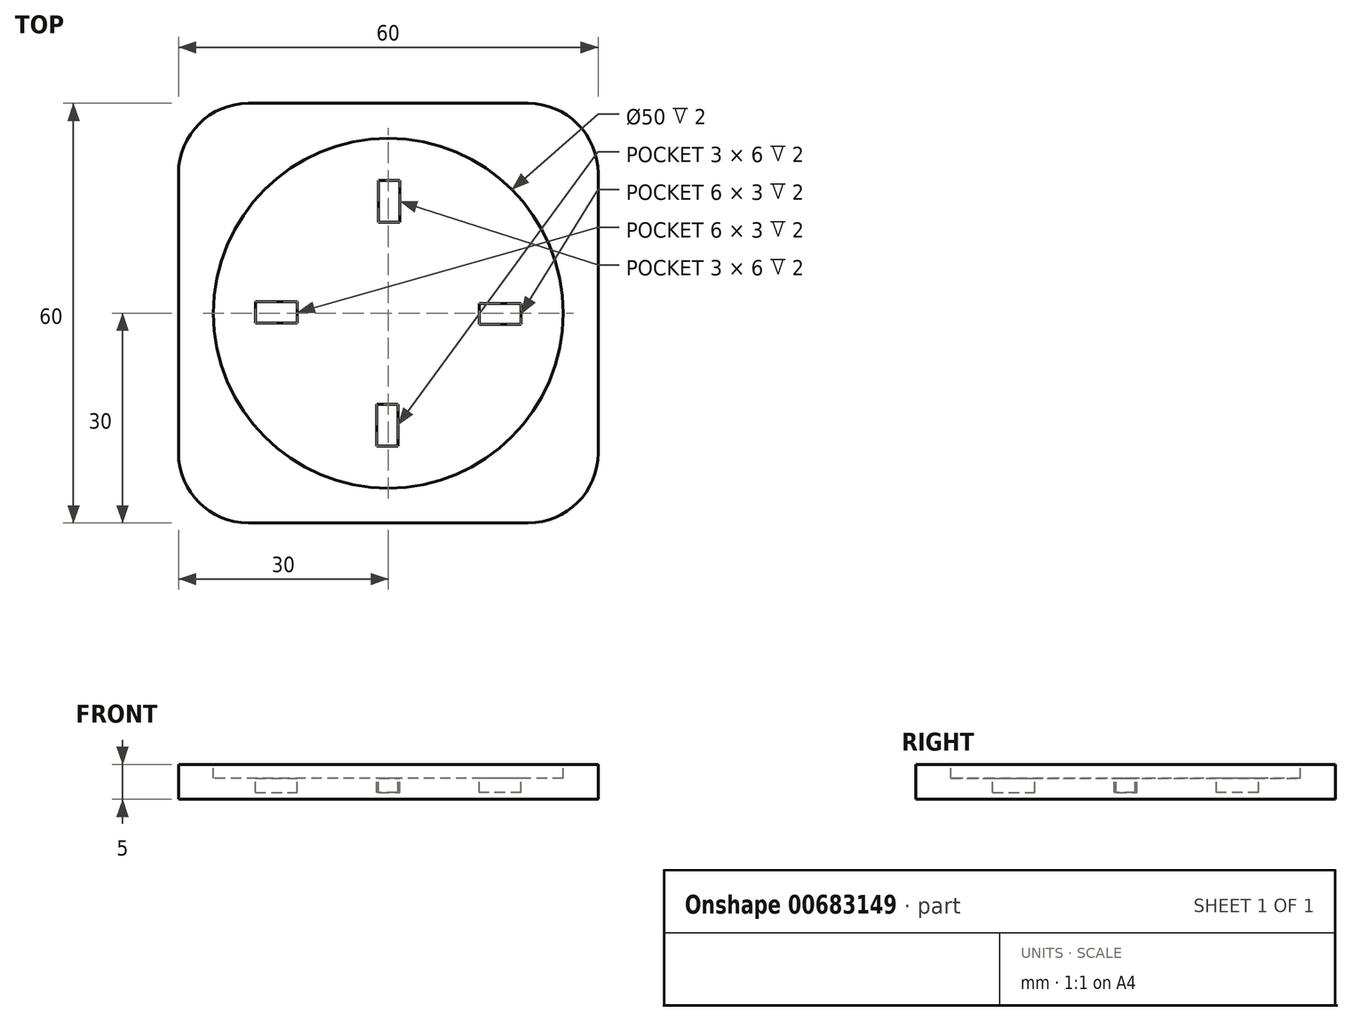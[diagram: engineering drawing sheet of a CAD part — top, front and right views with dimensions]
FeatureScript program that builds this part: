
annotation { "Feature Type Name" : "Feature", "Feature Type Description" : "" }
export const myFeature = defineFeature(function(context is Context, id is Id, definition is map)
    precondition{}
    {
        {
            var Q0;
            Q0=qCreatedBy(makeId("Top.planeOp"),FACE);
            var sketch = newSketch(context, id + "F0", { "sketchPlane" : qUnion([Q0])});
            skLineSegment(sketch, "E0.bottom", {"start": v(-20, 30) * mm, "end": v(20, 30) * mm});
            skLineSegment(sketch, "E0.top", {"start": v(-20, -30) * mm, "end": v(20, -30) * mm});
            skLineSegment(sketch, "E0.left", {"start": v(-30, 20) * mm, "end": v(-30, -20) * mm});
            skLineSegment(sketch, "E0.right", {"start": v(30, 20) * mm, "end": v(30, -20) * mm});
            skPoint(sketch, "E0.middle", {"position": v(0, 0) * mm});
            skPoint(sketch, "E1.visualSharp", {"position": v(-30, 30) * mm});
            skArc(sketch, "E1.filletArc", {"start": v(-20, 30) * mm, "mid": v(-27.07, 27.07) * mm, "end": v(-30, 20) * mm});
            skPoint(sketch, "E2.visualSharp", {"position": v(30, 30) * mm});
            skArc(sketch, "E2.filletArc", {"start": v(30, 20) * mm, "mid": v(27.07, 27.07) * mm, "end": v(20, 30) * mm});
            skPoint(sketch, "E3.visualSharp", {"position": v(-30, -30) * mm});
            skArc(sketch, "E3.filletArc", {"start": v(-30, -20) * mm, "mid": v(-27.07, -27.07) * mm, "end": v(-20, -30) * mm});
            skPoint(sketch, "E4.visualSharp", {"position": v(30, -30) * mm});
            skArc(sketch, "E4.filletArc", {"start": v(20, -30) * mm, "mid": v(27.07, -27.07) * mm, "end": v(30, -20) * mm});
            skSolve(sketch);
        }
        {
            var Q0;
            Q0=makeQuery(id+"F0.imprint","IMPRINT",FACE,{"disambiguationData":[TD([[makeQuery(id+"F0.imprint","IMPRINT",EDGE,{"derivedFrom":sQuery(id+"F0.wireOp",EDGE,"E0.bottom")}),-1.0]])]});
            extrude(context, id + "F1", {"entities" : qUnion([Q0]), "depth" : 5 * mm, "offsetDistance" : 25.4 * mm});
        }
        {
            var Q0;
            Q0=makeQuery(id+"F1.opExtrude","CAP_FACE",FACE,{"disambiguationData":[OSD([sQuery(id+"F0.wireOp",EDGE,"E0.bottom"),sQuery(id+"F0.wireOp",EDGE,"E0.top"),sQuery(id+"F0.wireOp",EDGE,"E0.left"),sQuery(id+"F0.wireOp",EDGE,"E0.right")])],"isStart":false});
            var sketch = newSketch(context, id + "F2", { "sketchPlane" : qUnion([Q0])});
            skCircle(sketch, "E5", {"center": v(0, 0) * mm, "radius": 25 * mm});
            skSolve(sketch);
        }
        {
            var Q0;
            Q0 = qSketchRegion(id + "F2", true);
            extrude(context, id + "F3", {"entities" : qUnion([Q0]), "operationType" : NewBodyOperationType.REMOVE, "oppositeDirection" : true, "depth" : 2 * mm, "offsetDistance" : 25.4 * mm});
        }
        {
            var Q0;
            Q0=makeQuery(id+"F3.boolean.opBoolean","COPY",FACE,{"derivedFrom":makeQuery(id+"F3.opExtrude","CAP_FACE",FACE,{"disambiguationData":[OSD([sQuery(id+"F2.wireOp",EDGE,"E5")])],"isStart":false})});
            var sketch = newSketch(context, id + "F4", { "sketchPlane" : qUnion([Q0])});
            skLineSegment(sketch, "E6.bottom", {"start": v(-1.37, 19) * mm, "end": v(1.63, 19) * mm});
            skLineSegment(sketch, "E6.top", {"start": v(-1.37, 13) * mm, "end": v(1.63, 13) * mm});
            skLineSegment(sketch, "E6.left", {"start": v(-1.37, 19) * mm, "end": v(-1.37, 13) * mm});
            skLineSegment(sketch, "E6.right", {"start": v(1.63, 19) * mm, "end": v(1.63, 13) * mm});
            skLineSegment(sketch, "E7.1.0", {"start": v(-19, -1.37) * mm, "end": v(-19, 1.63) * mm});
            skLineSegment(sketch, "E7.1.1", {"start": v(-19, -1.37) * mm, "end": v(-13, -1.37) * mm});
            skLineSegment(sketch, "E7.1.2", {"start": v(-19, 1.63) * mm, "end": v(-13, 1.63) * mm});
            skLineSegment(sketch, "E7.1.3", {"start": v(-13, -1.37) * mm, "end": v(-13, 1.63) * mm});
            skLineSegment(sketch, "E7.2.0", {"start": v(1.37, -19) * mm, "end": v(-1.63, -19) * mm});
            skLineSegment(sketch, "E7.2.1", {"start": v(1.37, -19) * mm, "end": v(1.37, -13) * mm});
            skLineSegment(sketch, "E7.2.2", {"start": v(-1.63, -19) * mm, "end": v(-1.63, -13) * mm});
            skLineSegment(sketch, "E7.2.3", {"start": v(1.37, -13) * mm, "end": v(-1.63, -13) * mm});
            skLineSegment(sketch, "E7.3.0", {"start": v(19, 1.37) * mm, "end": v(19, -1.63) * mm});
            skLineSegment(sketch, "E7.3.1", {"start": v(19, 1.37) * mm, "end": v(13, 1.37) * mm});
            skLineSegment(sketch, "E7.3.2", {"start": v(19, -1.63) * mm, "end": v(13, -1.63) * mm});
            skLineSegment(sketch, "E7.3.3", {"start": v(13, 1.37) * mm, "end": v(13, -1.63) * mm});
            skPoint(sketch, "E7.center", {"position": v(0, 0) * mm});
            skSolve(sketch);
        }
        {
            var Q0;
            Q0=makeQuery(id+"F4.imprint","IMPRINT",FACE,{"disambiguationData":[TD([[makeQuery(id+"F4.imprint","IMPRINT",EDGE,{"derivedFrom":sQuery(id+"F4.wireOp",EDGE,"E6.bottom")}),-1.0]])]});
            var Q1;
            Q1=makeQuery(id+"F4.imprint","IMPRINT",FACE,{"disambiguationData":[TD([[makeQuery(id+"F4.imprint","IMPRINT",EDGE,{"derivedFrom":sQuery(id+"F4.wireOp",EDGE,"E7.1.0")}),-1.0]])]});
            var Q2;
            Q2=makeQuery(id+"F4.imprint","IMPRINT",FACE,{"disambiguationData":[TD([[makeQuery(id+"F4.imprint","IMPRINT",EDGE,{"derivedFrom":sQuery(id+"F4.wireOp",EDGE,"E7.3.0")}),-1.0]])]});
            var Q3;
            Q3=makeQuery(id+"F4.imprint","IMPRINT",FACE,{"disambiguationData":[TD([[makeQuery(id+"F4.imprint","IMPRINT",EDGE,{"derivedFrom":sQuery(id+"F4.wireOp",EDGE,"E7.2.0")}),-1.0]])]});
            extrude(context, id + "F5", {"entities" : qUnion([Q0, Q1, Q2, Q3]), "operationType" : NewBodyOperationType.REMOVE, "oppositeDirection" : true, "depth" : 2 * mm, "offsetDistance" : 25.4 * mm});
        }
    });
